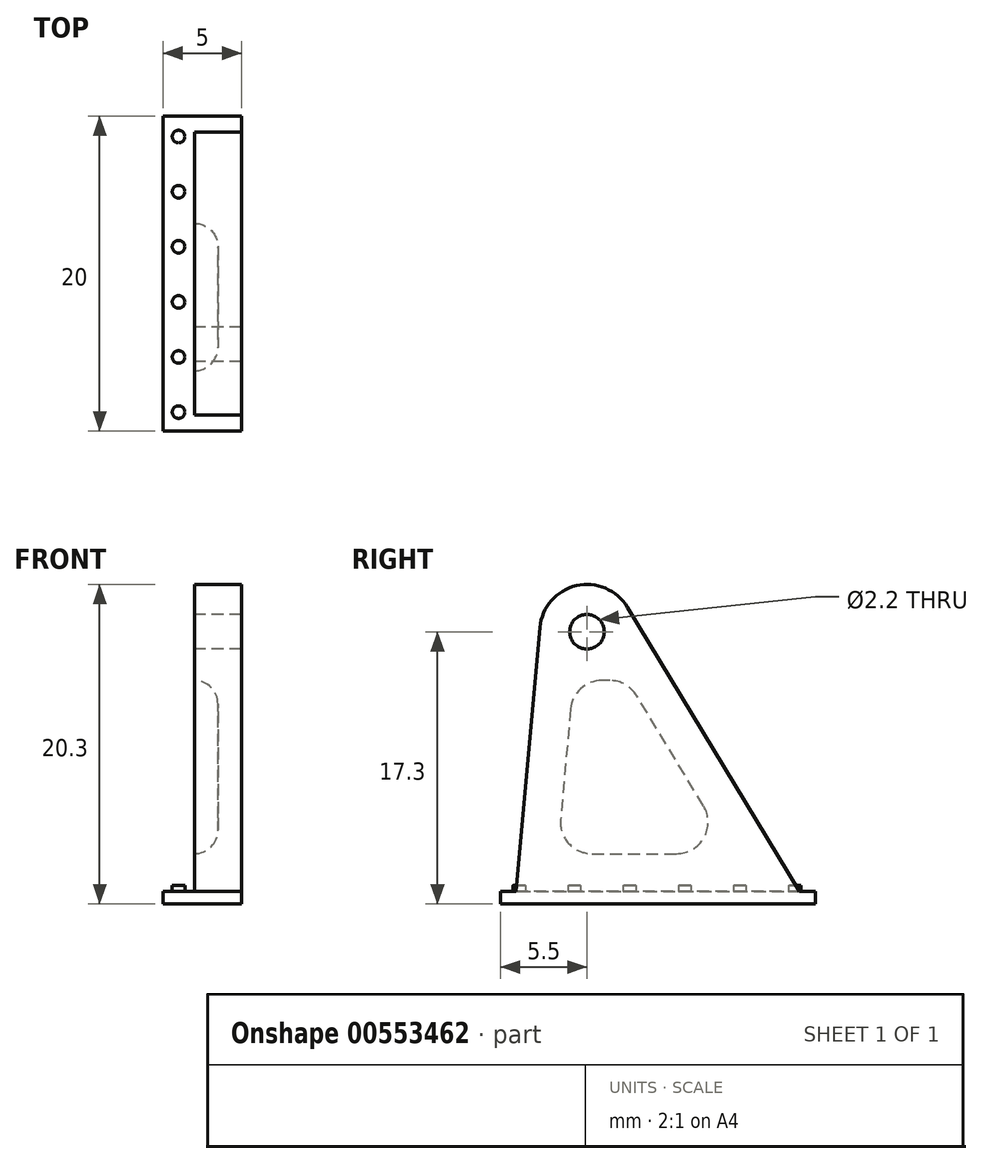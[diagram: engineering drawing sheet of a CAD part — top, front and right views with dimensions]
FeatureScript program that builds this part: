
annotation { "Feature Type Name" : "Feature", "Feature Type Description" : "" }
export const myFeature = defineFeature(function(context is Context, id is Id, definition is map)
    precondition{}
    {
        {
            var Q0;
            Q0=qCreatedBy(makeId("Right.planeOp"),FACE);
            var sketch = newSketch(context, id + "F0", { "sketchPlane" : qUnion([Q0])});
            skLineSegment(sketch, "E0.bottom", {"start": v(-5.5, 0) * mm, "end": v(14.5, 0) * mm});
            skLineSegment(sketch, "E0.top", {"start": v(-5.5, 0.8) * mm, "end": v(14.5, 0.8) * mm});
            skLineSegment(sketch, "E0.left", {"start": v(-5.5, 0) * mm, "end": v(-5.5, 0.8) * mm});
            skLineSegment(sketch, "E0.right", {"start": v(14.5, 0) * mm, "end": v(14.5, 0.8) * mm});
            skSolve(sketch);
        }
        {
            var Q0;
            Q0=qSketchRegion(id+"F0",true);
            extrude(context, id + "F1", {"entities" : qUnion([Q0]), "depth" : 3 * mm, "offsetDistance" : 25 * mm, "hasSecondDirection" : true, "secondDirectionOppositeDirection" : true, "secondDirectionDepth" : 2 * mm});
        }
        {
            var Q0;
            Q0=qCreatedBy(makeId("Right.planeOp"),FACE);
            var sketch = newSketch(context, id + "F2", { "sketchPlane" : qUnion([Q0])});
            skCircle(sketch, "E1", {"center": v(0, 17.3) * mm, "radius": 1.1 * mm});
            skLineSegment(sketch, "E2.0", {"start": v(-5.5, 0.8) * mm, "end": v(14.5, 0.8) * mm, "construction": true});
            skLineSegment(sketch, "E3", {"start": v(13.5, 0.8) * mm, "end": v(2.57, 18.85) * mm});
            skLineSegment(sketch, "E4", {"start": v(13.5, 0.8) * mm, "end": v(-4.5, 0.8) * mm});
            skLineSegment(sketch, "E5", {"start": v(-4.5, 0.8) * mm, "end": v(-2.99, 17.57) * mm});
            skArc(sketch, "E6", {"start": v(2.57, 18.85) * mm, "mid": v(-0.68, 20.22) * mm, "end": v(-2.99, 17.57) * mm});
            skSolve(sketch);
        }
        {
            var Q0;
            Q0=qSketchRegion(id+"F2",true);
            extrude(context, id + "F3", {"entities" : qUnion([Q0]), "operationType" : NewBodyOperationType.ADD, "depth" : 3 * mm, "offsetDistance" : 25 * mm});
        }
        {
            var Q0;
            Q0=makeQuery(id+"F3.opExtrude","CAP_FACE",FACE,{"disambiguationData":[OSD([sQuery(id+"F2.wireOp",EDGE,"E1"),sQuery(id+"F2.wireOp",EDGE,"E3"),sQuery(id+"F2.wireOp",EDGE,"E4"),sQuery(id+"F2.wireOp",EDGE,"E5"),sQuery(id+"F2.wireOp",EDGE,"E6")])],"isStart":true});
            var sketch = newSketch(context, id + "F4", { "sketchPlane" : qUnion([Q0])});
            skLineSegment(sketch, "E7", {"start": v(1.87, 3.2) * mm, "end": v(-9.24, 3.2) * mm});
            skLineSegment(sketch, "E8", {"start": v(-9.24, 3.2) * mm, "end": v(-2.58, 14.2) * mm});
            skLineSegment(sketch, "E9", {"start": v(-2.58, 14.2) * mm, "end": v(0.88, 14.2) * mm});
            skLineSegment(sketch, "E10", {"start": v(0.88, 14.2) * mm, "end": v(1.87, 3.2) * mm});
            skSolve(sketch);
        }
        {
            var Q0;
            Q0=qSketchRegion(id+"F4",true);
            extrude(context, id + "F5", {"entities" : qUnion([Q0]), "operationType" : NewBodyOperationType.REMOVE, "oppositeDirection" : true, "depth" : 1.5 * mm, "offsetDistance" : 25 * mm});
        }
        {
            var Q0;
            Q0=makeQuery(id+"F5.boolean.opBoolean","COPY",EDGE,{"derivedFrom":makeQuery(id+"F5.opExtrude","SWEPT_EDGE",EDGE,{"disambiguationData":[OSD([sQuery(id+"F4.wireOp",EDGE,"E9"),sQuery(id+"F4.wireOp",EDGE,"E10")])]})});
            var Q1;
            Q1=makeQuery(id+"F5.boolean.opBoolean","COPY",EDGE,{"derivedFrom":makeQuery(id+"F5.opExtrude","SWEPT_EDGE",EDGE,{"disambiguationData":[OSD([sQuery(id+"F4.wireOp",EDGE,"E8"),sQuery(id+"F4.wireOp",EDGE,"E9")])]})});
            var Q2;
            Q2=makeQuery(id+"F5.boolean.opBoolean","COPY",EDGE,{"derivedFrom":makeQuery(id+"F5.opExtrude","SWEPT_EDGE",EDGE,{"disambiguationData":[OSD([sQuery(id+"F4.wireOp",EDGE,"E7"),sQuery(id+"F4.wireOp",EDGE,"E8")])]})});
            var Q3;
            Q3=makeQuery(id+"F5.boolean.opBoolean","COPY",EDGE,{"derivedFrom":makeQuery(id+"F5.opExtrude","SWEPT_EDGE",EDGE,{"disambiguationData":[OSD([sQuery(id+"F4.wireOp",EDGE,"E7"),sQuery(id+"F4.wireOp",EDGE,"E10")])]})});
            fillet(context, id + "F6", {"entities" : qUnion([Q0, Q1, Q2, Q3]), "radius" : 2 * mm, "tangentPropagation" : true, "allowEdgeOverflow" : false});
        }
        {
            var Q0;
            Q0=makeQuery(id+"F5.boolean.opBoolean","COPY",FACE,{"derivedFrom":makeQuery(id+"F5.opExtrude","CAP_FACE",FACE,{"disambiguationData":[OSD([sQuery(id+"F4.wireOp",EDGE,"E7"),sQuery(id+"F4.wireOp",EDGE,"E8"),sQuery(id+"F4.wireOp",EDGE,"E9"),sQuery(id+"F4.wireOp",EDGE,"E10")])],"isStart":false})});
            fillet(context, id + "F7", {"entities" : qUnion([Q0]), "radius" : 1.5 * mm, "tangentPropagation" : true, "allowEdgeOverflow" : false});
        }
        {
            var Q0;
            Q0=makeQuery(id+"F1.opExtrude","SWEPT_FACE",FACE,{"disambiguationData":[OSD([sQuery(id+"F0.wireOp",EDGE,"E0.top")])]});
            var sketch = newSketch(context, id + "F8", { "sketchPlane" : qUnion([Q0])});
            skCircle(sketch, "E11", {"center": v(-1, -4.3) * mm, "radius": 0.4 * mm});
            skCircle(sketch, "E12.1.0.0", {"center": v(-1, -0.8) * mm, "radius": 0.4 * mm});
            skCircle(sketch, "E12.2.0.0", {"center": v(-1, 2.7) * mm, "radius": 0.4 * mm});
            skCircle(sketch, "E12.3.0.0", {"center": v(-1, 6.2) * mm, "radius": 0.4 * mm});
            skCircle(sketch, "E12.4.0.0", {"center": v(-1, 9.7) * mm, "radius": 0.4 * mm});
            skCircle(sketch, "E12.5.0.0", {"center": v(-1, 13.2) * mm, "radius": 0.4 * mm});
            skLineSegment(sketch, "E12.direction1", {"start": v(-1, -4.3) * mm, "end": v(-1, -0.8) * mm, "construction": true});
            skSolve(sketch);
        }
        {
            var Q0;
            Q0 = qSketchRegion(id + "F8", true);
            extrude(context, id + "F9", {"entities" : qUnion([Q0]), "operationType" : NewBodyOperationType.ADD, "depth" : 0.4 * mm, "offsetDistance" : 25 * mm});
        }
    });
